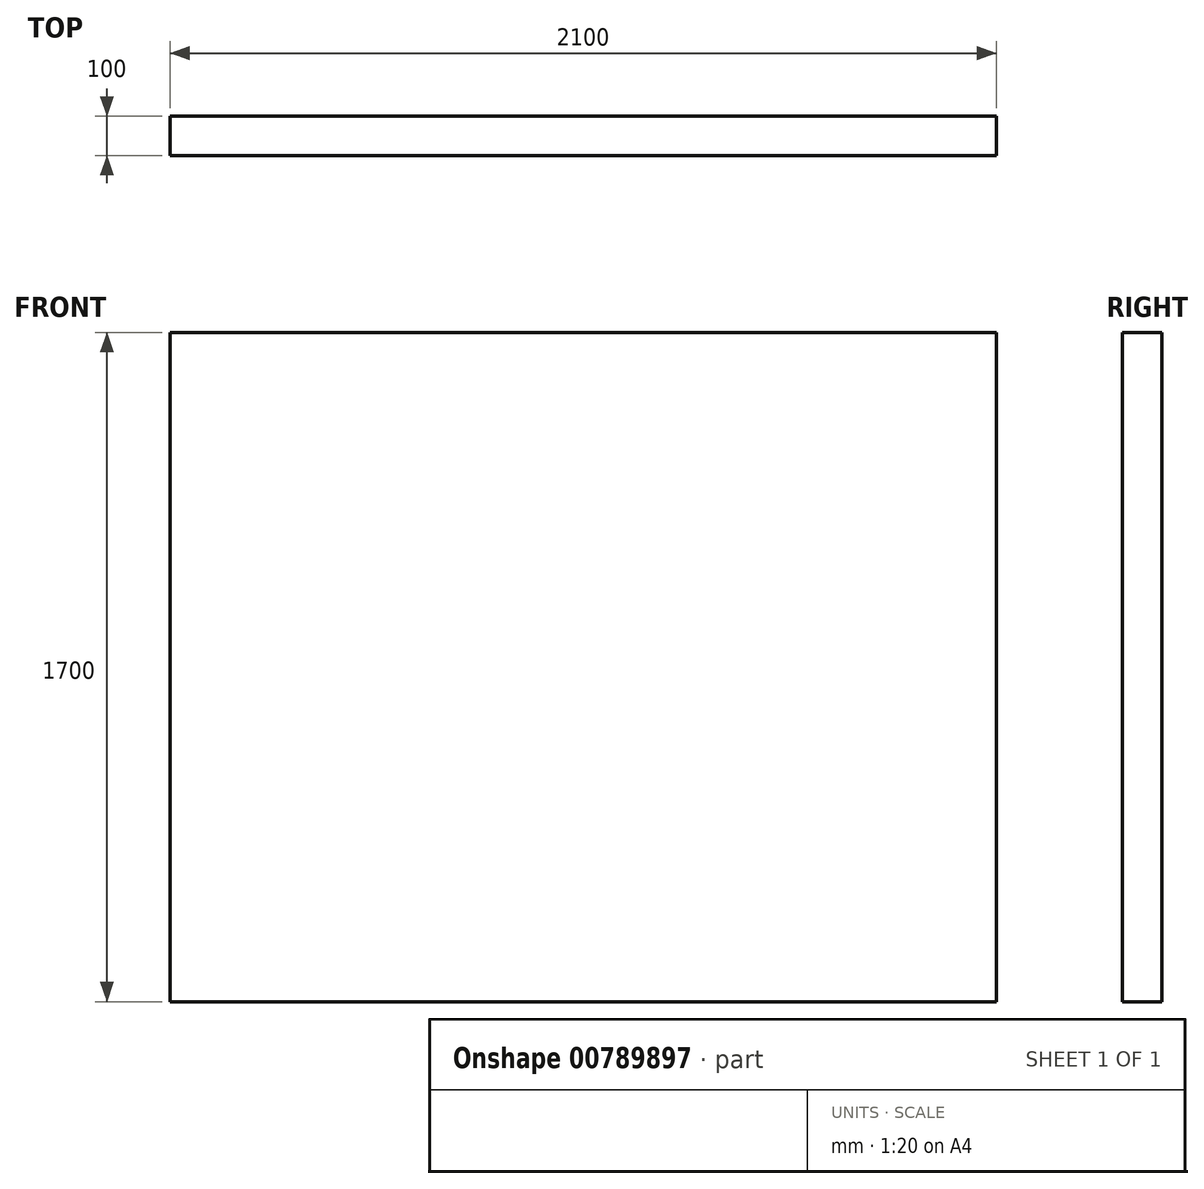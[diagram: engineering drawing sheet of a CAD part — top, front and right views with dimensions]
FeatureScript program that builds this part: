
annotation { "Feature Type Name" : "Feature", "Feature Type Description" : "" }
export const myFeature = defineFeature(function(context is Context, id is Id, definition is map)
    precondition{}
    {
        {
            var Q0;
            Q0=qCreatedBy(makeId("Top.planeOp"),FACE);
            var sketch = newSketch(context, id + "F0", { "sketchPlane" : qUnion([Q0])});
            skLineSegment(sketch, "E0.bottom", {"start": v(-65.06, 91.81) * mm, "end": v(2034.94, 91.81) * mm});
            skLineSegment(sketch, "E0.top", {"start": v(-65.06, -8.19) * mm, "end": v(2034.94, -8.19) * mm});
            skLineSegment(sketch, "E0.left", {"start": v(-65.06, 91.81) * mm, "end": v(-65.06, -8.19) * mm});
            skLineSegment(sketch, "E0.right", {"start": v(2034.94, 91.81) * mm, "end": v(2034.94, -8.19) * mm});
            skSolve(sketch);
        }
        {
            var Q0;
            Q0 = qSketchRegion(id + "F0", true);
            extrude(context, id + "F1", {"entities" : qUnion([Q0]), "depth" : 1700 * mm, "offsetDistance" : 25 * mm});
        }
    });
